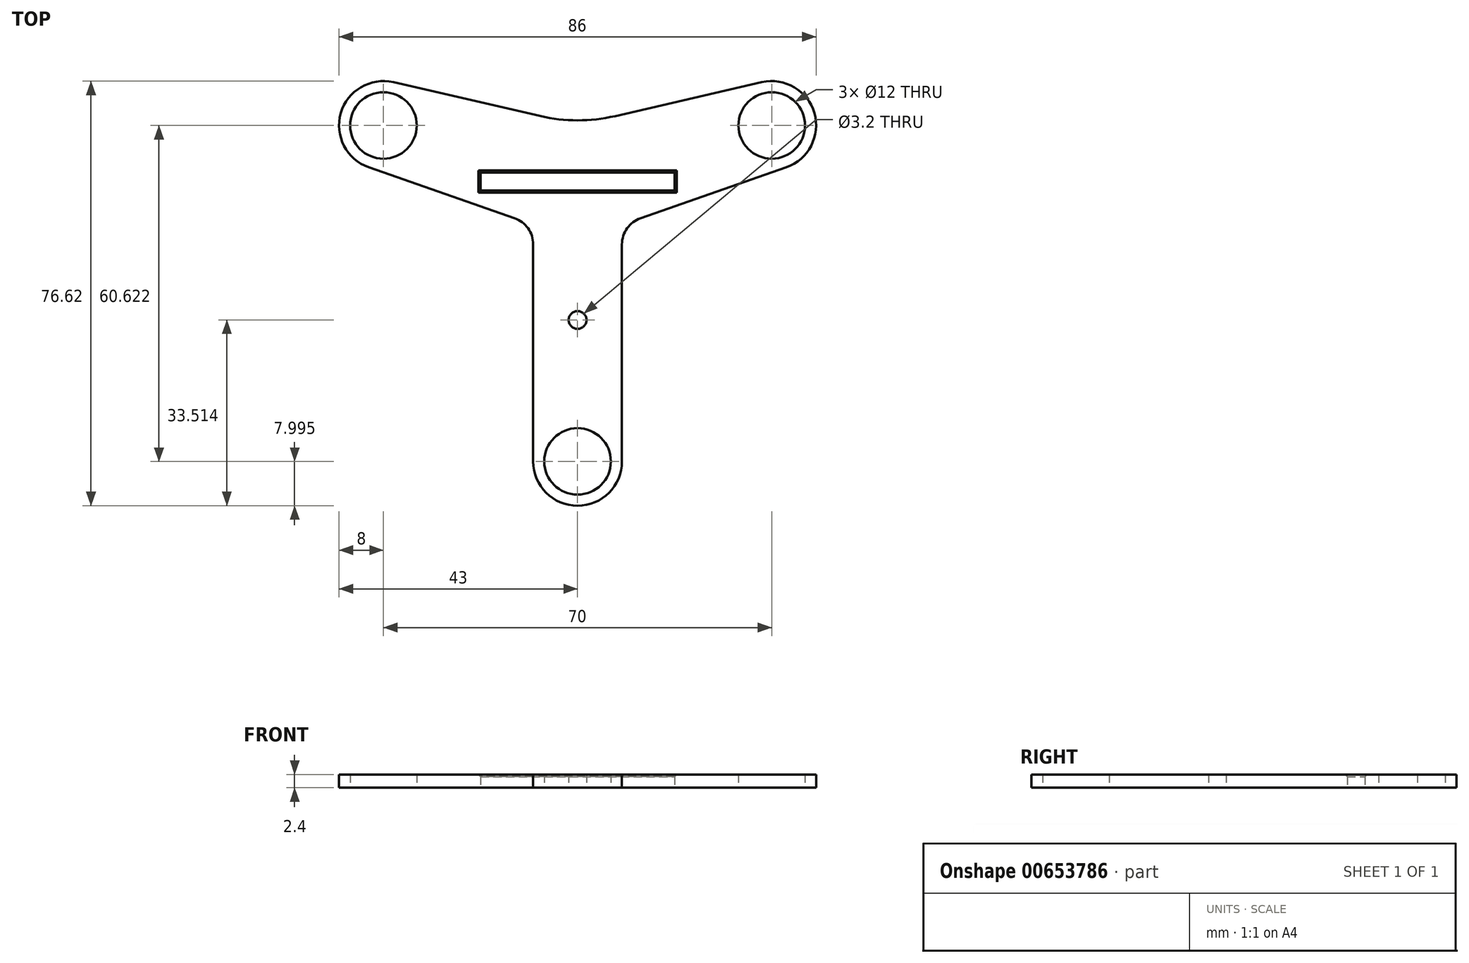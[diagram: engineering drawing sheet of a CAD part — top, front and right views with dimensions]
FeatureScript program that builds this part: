
annotation { "Feature Type Name" : "Feature", "Feature Type Description" : "" }
export const myFeature = defineFeature(function(context is Context, id is Id, definition is map)
    precondition{}
    {
        {
            var Q0;
            Q0=qCreatedBy(makeId("Top.planeOp"),FACE);
            var sketch = newSketch(context, id + "F0", { "sketchPlane" : qUnion([Q0])});
            skArc(sketch, "E0.cCircle", {"start": v(-6, -39.97) * mm, "mid": v(-6, -39.97) * mm, "end": v(-5.98, -39.97) * mm, "construction": true});
            skCircle(sketch, "E1", {"center": v(35, 20.2) * mm, "radius": 6 * mm});
            skCircle(sketch, "E2", {"center": v(-35, 20.2) * mm, "radius": 6 * mm});
            skArc(sketch, "E3", {"start": v(-8, -40.41) * mm, "mid": v(0, -48.41) * mm, "end": v(8, -40.41) * mm});
            skArc(sketch, "E4", {"start": v(-33.2, 28) * mm, "mid": v(-42.69, 22.43) * mm, "end": v(-37.64, 12.65) * mm});
            skArc(sketch, "E5", {"start": v(37.64, 12.65) * mm, "mid": v(42.69, 22.43) * mm, "end": v(33.2, 28) * mm});
            skCircle(sketch, "E6", {"center": v(0, -40.41) * mm, "radius": 6 * mm});
            skLineSegment(sketch, "E7.bottom", {"start": v(17.5, 8.5) * mm, "end": v(-17.5, 8.5) * mm});
            skLineSegment(sketch, "E7.top", {"start": v(17.5, 11.7) * mm, "end": v(-17.5, 11.7) * mm});
            skLineSegment(sketch, "E7.left", {"start": v(17.5, 8.5) * mm, "end": v(17.5, 11.7) * mm});
            skLineSegment(sketch, "E7.right", {"start": v(-17.5, 8.5) * mm, "end": v(-17.5, 11.7) * mm});
            skPoint(sketch, "E7.middle", {"position": v(0, 10.1) * mm});
            skArc(sketch, "E8.trimOffspring", {"start": v(5.98, -39.97) * mm, "mid": v(6, -39.97) * mm, "end": v(6, -39.97) * mm, "construction": true});
            skCircle(sketch, "E9", {"center": v(0, -14.9) * mm, "radius": 1.6 * mm});
            skLineSegment(sketch, "E10", {"start": v(-33.2, 28) * mm, "end": v(0, 20.35) * mm});
            skLineSegment(sketch, "E11", {"start": v(-37.64, 12.65) * mm, "end": v(-8, 2.3) * mm});
            skLineSegment(sketch, "E12", {"start": v(33.2, 28) * mm, "end": v(0, 20.35) * mm});
            skLineSegment(sketch, "E13", {"start": v(37.64, 12.65) * mm, "end": v(8, 2.3) * mm});
            skPoint(sketch, "E14.orphan", {"position": v(-1.4, 0) * mm});
            skLineSegment(sketch, "E15", {"start": v(-8, 2.3) * mm, "end": v(-8, -40.41) * mm});
            skLineSegment(sketch, "E16", {"start": v(8, 2.3) * mm, "end": v(8, -40.41) * mm});
            skSolve(sketch);
        }
        {
            var Q0;
            Q0 = qSketchRegion(id + "F0", true);
            extrude(context, id + "F1", {"entities" : qUnion([Q0]), "depth" : 2.4 * mm, "offsetDistance" : 25 * mm});
        }
        {
            var Q0;
            Q0=makeQuery(id+"F1.opExtrude","CAP_EDGE",EDGE,{"disambiguationData":[OSD([sQuery(id+"F0.wireOp",EDGE,"E7.right")])],"isStart":false});
            var Q1;
            Q1=makeQuery(id+"F1.opExtrude","CAP_EDGE",EDGE,{"disambiguationData":[OSD([sQuery(id+"F0.wireOp",EDGE,"E7.top")])],"isStart":false});
            var Q2;
            Q2=makeQuery(id+"F1.opExtrude","CAP_EDGE",EDGE,{"disambiguationData":[OSD([sQuery(id+"F0.wireOp",EDGE,"E7.bottom")])],"isStart":false});
            var Q3;
            Q3=makeQuery(id+"F1.opExtrude","CAP_EDGE",EDGE,{"disambiguationData":[OSD([sQuery(id+"F0.wireOp",EDGE,"E7.left")])],"isStart":false});
            chamfer(context, id + "F2", {"entities" : qUnion([Q0, Q1, Q2, Q3]), "width" : 0.4 * mm, "tangentPropagation" : true});
        }
        {
            var Q0;
            Q0=makeQuery(id+"F1.opExtrude","SWEPT_EDGE",EDGE,{"disambiguationData":[OSD([sQuery(id+"F0.wireOp",EDGE,"E10"),sQuery(id+"F0.wireOp",EDGE,"E12")])]});
            fillet(context, id + "F3", {"entities" : qUnion([Q0]), "radius" : 30 * mm, "tangentPropagation" : true, "allowEdgeOverflow" : false});
        }
        {
            var Q0;
            Q0=makeQuery(id+"F1.opExtrude","SWEPT_EDGE",EDGE,{"disambiguationData":[OSD([sQuery(id+"F0.wireOp",EDGE,"E11"),sQuery(id+"F0.wireOp",EDGE,"kkyDODQq-NWPm-T9zo-Psj0-zab0bg4iHysX")])]});
            var Q1;
            Q1=makeQuery(id+"F1.opExtrude","SWEPT_EDGE",EDGE,{"disambiguationData":[OSD([sQuery(id+"F0.wireOp",EDGE,"E13"),sQuery(id+"F0.wireOp",EDGE,"TzCoqYS7-AXv9-AlpY-eKIi-6r1YGYhNtSbE")])]});
            fillet(context, id + "F4", {"entities" : qUnion([Q0, Q1]), "radius" : 5 * mm, "tangentPropagation" : true, "allowEdgeOverflow" : false});
        }
    });
